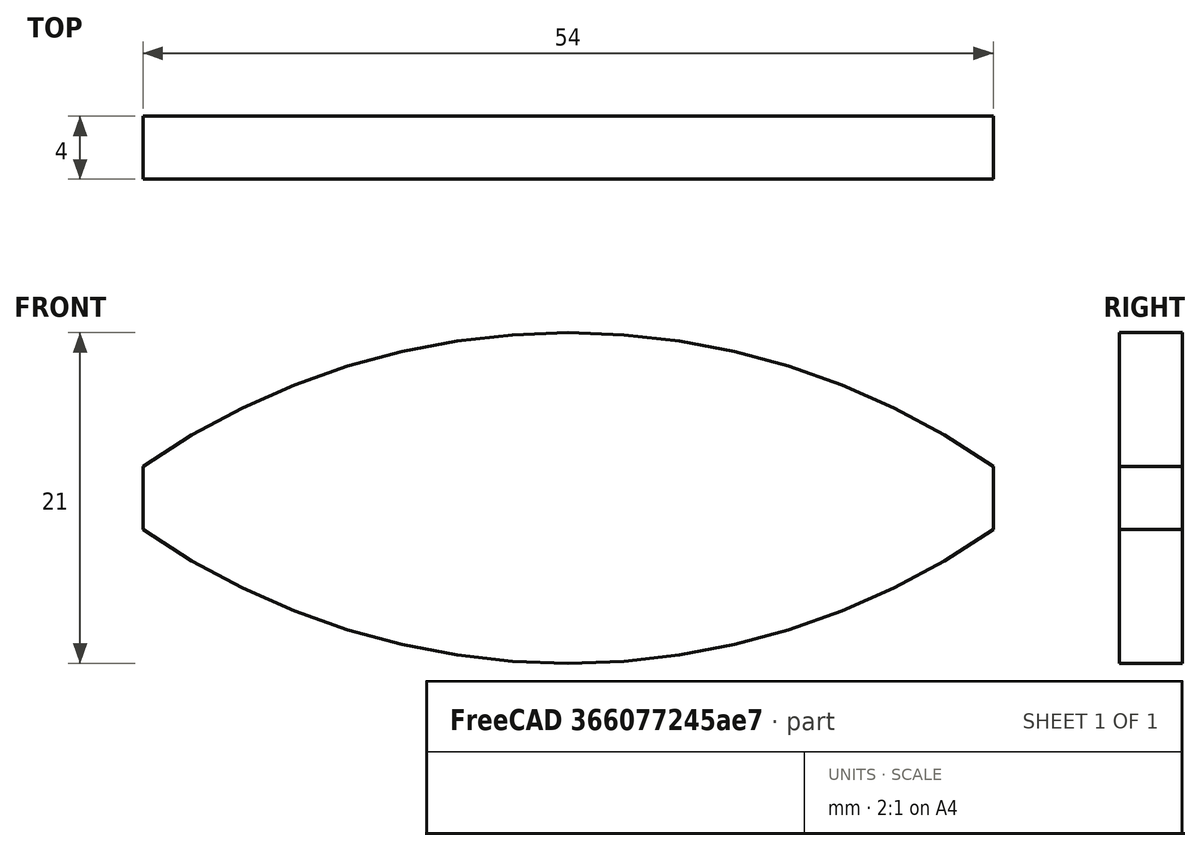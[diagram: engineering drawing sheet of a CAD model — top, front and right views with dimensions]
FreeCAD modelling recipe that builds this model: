
FCSTD DOCUMENT  (FreeCAD 1.1R20260325 (Git shallow))
Label: Biscuits_4_x_21_x_54_mm
License: All rights reserved
LicenseURL: http://en.wikipedia.org/wiki/All_rights_reserved
objects: App::LinkGroup×2, App::Point×2, Sketcher::SketchObject×1, Spreadsheet::Sheet×1, PartDesign::Pad×1, PartDesign::Body×1, App::Part×1
note: 6 computed .brp shape members not serialized (recipe doc carries the construction recipe); baked Part::Feature solids carry a one-line shape summary decoded from their .brp

FEATURE [Sketcher::SketchObject] Sketch
  ArcFitTolerance = 0
  AttachmentSupport = -> [XZ_Plane001]
  ExternalTypes = [0]
  FullyConstrained = false
  MakeInternals = false
  MapMode = 5
  Placement = pos=(0,0,0) rot=(1,0,0;1.5708rad)
  _ExternalGeoVersion = 0
  expr: Constraints[13] = <<settings>>.bw
  expr: Constraints[14] = <<settings>>.bh
  expr: Constraints[16] = <<settings>>.bw / 2
  sketch-geometry (6):
    g0: LineSegment StartX=-27 StartY=12.5 StartZ=0 EndX=-27 EndY=8.5 EndZ=0
    g1: LineSegment StartX=27 StartY=12.5 StartZ=0 EndX=27 EndY=8.5 EndZ=0
    g2: ArcOfCircle CenterX=0 CenterY=-26.1324 CenterZ=0 NormalX=0 NormalY=0 NormalZ=1 AngleXU=0 Radius=47.1324 StartAngle=0.960812 EndAngle=2.18078
    g3: ArcOfCircle CenterX=0 CenterY=47.1324 CenterZ=0 NormalX=0 NormalY=0 NormalZ=1 AngleXU=0 Radius=47.1324 StartAngle=4.1024 EndAngle=5.32237
    g4: LineSegment [constr] StartX=0 StartY=21 StartZ=0 EndX=0 EndY=0 EndZ=0
    g5: LineSegment [constr] StartX=-49.5813 StartY=10.5 StartZ=0 EndX=66.2857 EndY=10.5 EndZ=0
  constraints (18):
    c: Vertical(g0)
    c: Vertical(g1)
    c: Coincident(g2,g0)
    c: Coincident(g2,g1)
    c: Coincident(g3,g0)
    c: Coincident(g3,g1)
    c: PointOnObject(g4,g2)
    c: PointOnObject(g4,g3)
    c: Vertical(g4)
    c: Coincident(g4,g-1)
    c: Horizontal(g1,g0)
    c: DistanceY(g1,g1) = 4
    c: Vertical(g3,g4)
    c: DistanceY(g4,g4) = 21
    c: DistanceX(g0,g1) = 54
    c: Horizontal(g5)
    c: DistanceY(g4,g5) = 10.5
    c: Symmetric(g2,g3,g5)
FEATURE [Spreadsheet::Sheet] Spreadsheet  label="settings"
  cells = A1='Settings:; A2='Width; B2(bw)=21; A3='Height; B3(bh)=54
FEATURE [PartDesign::Pad] Pad
  Direction = (0,-1,2e-16)
  Length = 4
  Length2 = 10
  Placement = pos=(0,0,0) rot=(1,0,0;1.5708rad)
  Profile = -> Sketch
  ReferenceAxis = -> Sketch [N_Axis]
  SideType = 0
  Suppressed = false
  Type = 0
  Type2 = 0
FEATURE [PartDesign::Body] Body
  AllowCompound = true
  Group = -> [Sketch,Pad]
  Origin = -> Origin001
  Placement = pos=(0,2,0) rot=(0,0,1;0rad)
  Tip = -> Pad
FEATURE [App::Part] Part
  Group = -> [Body]
  Origin = -> Origin
FEATURE [App::LinkGroup] LinkGroup  label="Biscuits 4 x 21 x 54 mm, link this"
  ElementList = -> [Part]
  LinkMode = 0
FEATURE [App::LinkGroup] LinkGroup001  label="Biscuits 4 x 21 x 54 mm, hide this"
  ElementList = -> [LinkGroup]
  LinkMode = 0
FEATURE [App::Point] Origin002  label="Origin"
  Role = Origin
FEATURE [App::Point] Origin003  label="Origin"
  Role = Origin
